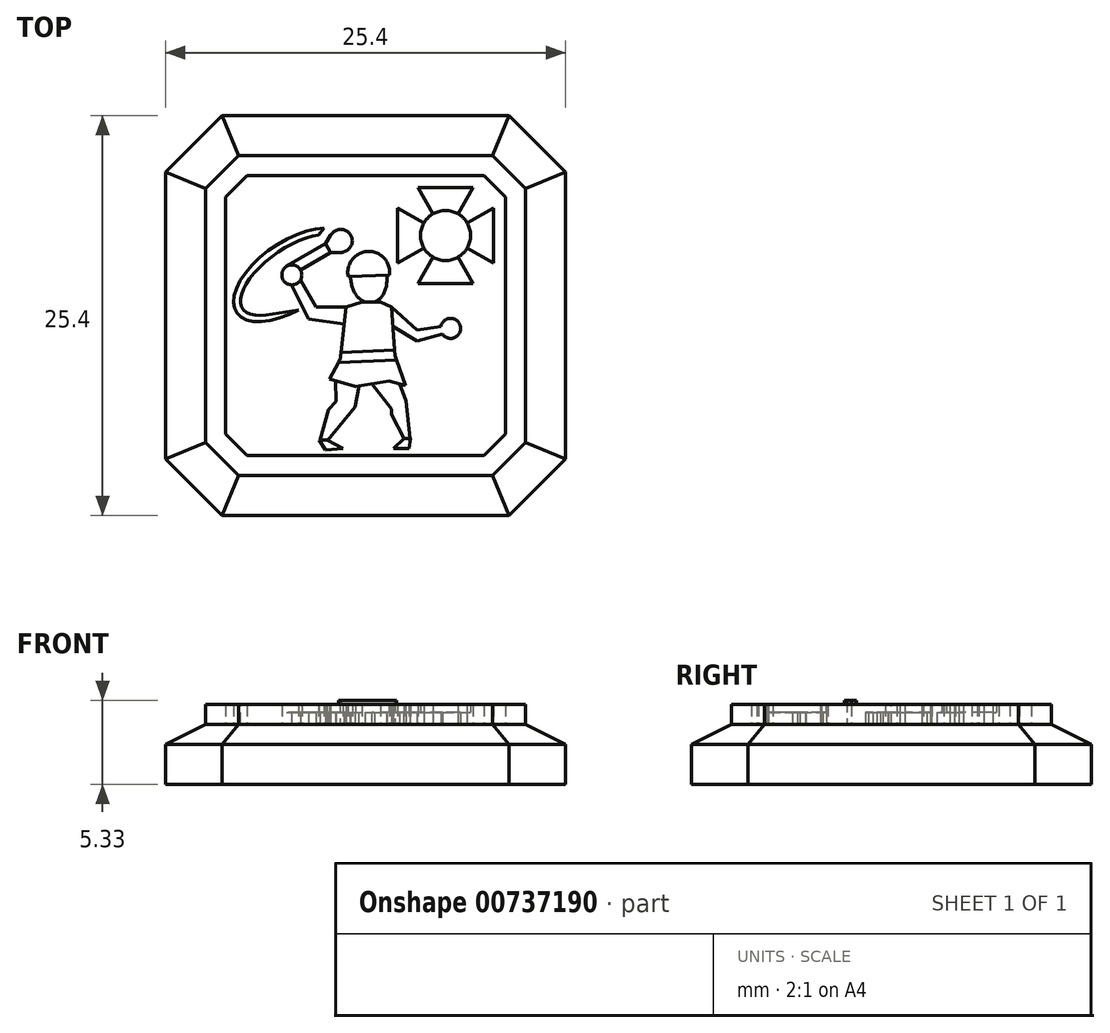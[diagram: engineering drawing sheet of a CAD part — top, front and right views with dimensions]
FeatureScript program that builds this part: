
annotation { "Feature Type Name" : "Feature", "Feature Type Description" : "" }
export const myFeature = defineFeature(function(context is Context, id is Id, definition is map)
    precondition{}
    {
        {
            var Q0;
            Q0=qCreatedBy(makeId("Top.planeOp"),FACE);
            var sketch = newSketch(context, id + "F0", { "sketchPlane" : qUnion([Q0])});
            skLineSegment(sketch, "E0", {"start": v(0, 34.78) * mm, "end": v(0, -32.67) * mm, "construction": true});
            skLineSegment(sketch, "E1", {"start": v(-47.17, 0) * mm, "end": v(41.3, 0) * mm});
            skLineSegment(sketch, "E2", {"start": v(0, 12.7) * mm, "end": v(-9.1, 12.7) * mm});
            skLineSegment(sketch, "E3", {"start": v(-9.1, 12.7) * mm, "end": v(-12.7, 9.1) * mm});
            skLineSegment(sketch, "E4", {"start": v(-12.7, 9.1) * mm, "end": v(-12.7, 0) * mm});
            skLineSegment(sketch, "E5.MirrorCS", {"start": v(0, 12.7) * mm, "end": v(9.1, 12.7) * mm});
            skLineSegment(sketch, "E6.MirrorCS", {"start": v(9.1, 12.7) * mm, "end": v(12.7, 9.1) * mm});
            skLineSegment(sketch, "E7.MirrorCS", {"start": v(12.7, 9.1) * mm, "end": v(12.7, 0) * mm});
            skLineSegment(sketch, "E8.MirrorCS", {"start": v(12.7, -9.1) * mm, "end": v(12.7, 0) * mm});
            skLineSegment(sketch, "E9.MirrorCS", {"start": v(9.1, -12.7) * mm, "end": v(12.7, -9.1) * mm});
            skLineSegment(sketch, "E10.MirrorCS", {"start": v(0, -12.7) * mm, "end": v(9.1, -12.7) * mm});
            skLineSegment(sketch, "E11.MirrorCS", {"start": v(0, -12.7) * mm, "end": v(-9.1, -12.7) * mm});
            skLineSegment(sketch, "E12.MirrorCS", {"start": v(-9.1, -12.7) * mm, "end": v(-12.7, -9.1) * mm});
            skLineSegment(sketch, "E13.MirrorCS", {"start": v(-12.7, -9.1) * mm, "end": v(-12.7, 0) * mm});
            skSolve(sketch);
        }
        {
            var Q0;
            Q0=makeQuery(id+"F0.imprint","IMPRINT",FACE,{"disambiguationData":[TD([[makeQuery(id+"F0.imprint","IMPRINT",EDGE,{"derivedFrom":sQuery(id+"F0.wireOp",EDGE,"E2")}),1.0]])]});
            var Q1;
            {var subQ0=sQuery(id+"F0.wireOp",EDGE,"E8.MirrorCS");Q1=makeQuery(id+"F0.imprint","IMPRINT",FACE,{"disambiguationData":[TD([[makeQuery(id+"F0.imprint","IMPRINT",EDGE,{"derivedFrom":subQ0}),1.0]])]});}
            extrude(context, id + "F1", {"entities" : qUnion([Q0, Q1]), "depth" : 3.8 * mm, "offsetDistance" : 25.4 * mm});
        }
        {
            var Q0;
            Q0=makeQuery(id+"F1.opExtrude","CAP_EDGE",EDGE,{"disambiguationData":[OSD([sQuery(id+"F0.wireOp",EDGE,"E10.MirrorCS"),sQuery(id+"F0.wireOp",EDGE,"E11.MirrorCS")])],"isStart":false});
            var Q1;
            Q1=makeQuery(id+"F1.opExtrude","CAP_EDGE",EDGE,{"disambiguationData":[OSD([sQuery(id+"F0.wireOp",EDGE,"E4"),sQuery(id+"F0.wireOp",EDGE,"E13.MirrorCS")])],"isStart":false});
            var Q2;
            Q2=makeQuery(id+"F1.opExtrude","CAP_EDGE",EDGE,{"disambiguationData":[OSD([sQuery(id+"F0.wireOp",EDGE,"E2"),sQuery(id+"F0.wireOp",EDGE,"E5.MirrorCS")])],"isStart":false});
            var Q3;
            Q3=makeQuery(id+"F1.opExtrude","CAP_EDGE",EDGE,{"disambiguationData":[OSD([sQuery(id+"F0.wireOp",EDGE,"E7.MirrorCS"),sQuery(id+"F0.wireOp",EDGE,"E8.MirrorCS")])],"isStart":false});
            var Q4;
            Q4=makeQuery(id+"F1.opExtrude","CAP_EDGE",EDGE,{"disambiguationData":[OSD([sQuery(id+"F0.wireOp",EDGE,"E6.MirrorCS")])],"isStart":false});
            var Q5;
            Q5=makeQuery(id+"F1.opExtrude","CAP_EDGE",EDGE,{"disambiguationData":[OSD([sQuery(id+"F0.wireOp",EDGE,"E3")])],"isStart":false});
            var Q6;
            Q6=makeQuery(id+"F1.opExtrude","CAP_EDGE",EDGE,{"disambiguationData":[OSD([sQuery(id+"F0.wireOp",EDGE,"E9.MirrorCS")])],"isStart":false});
            var Q7;
            Q7=makeQuery(id+"F1.opExtrude","CAP_EDGE",EDGE,{"disambiguationData":[OSD([sQuery(id+"F0.wireOp",EDGE,"E12.MirrorCS")])],"isStart":false});
            chamfer(context, id + "F2", {"entities" : qUnion([Q0, Q1, Q2, Q3, Q4, Q5, Q6, Q7]), "chamferType" : ChamferType.TWO_OFFSETS, "width1" : 1.27 * mm, "oppositeDirection" : false, "width2" : 2.54 * mm, "tangentPropagation" : true});
        }
        {
            var Q0;
            Q0=qCreatedBy(makeId("Top.planeOp"),FACE);
            var sketch = newSketch(context, id + "F3", { "sketchPlane" : qUnion([Q0])});
            skLineSegment(sketch, "E14", {"start": v(-10.16, 8.06) * mm, "end": v(-8.06, 10.16) * mm});
            skLineSegment(sketch, "E15", {"start": v(-8.06, 10.16) * mm, "end": v(0, 10.16) * mm});
            skLineSegment(sketch, "E16", {"start": v(-10.16, 8.06) * mm, "end": v(-10.16, 0) * mm});
            skLineSegment(sketch, "E17", {"start": v(-15.43, 0) * mm, "end": v(15.43, 0) * mm, "construction": true});
            skLineSegment(sketch, "E18", {"start": v(0, 15.6) * mm, "end": v(0, -14.81) * mm, "construction": true});
            skLineSegment(sketch, "E19.MirrorCS", {"start": v(8.06, 10.16) * mm, "end": v(0, 10.16) * mm});
            skLineSegment(sketch, "E20.MirrorCS", {"start": v(10.16, 8.06) * mm, "end": v(8.06, 10.16) * mm});
            skLineSegment(sketch, "E21.MirrorCS", {"start": v(10.16, 8.06) * mm, "end": v(10.16, 0) * mm});
            skLineSegment(sketch, "E22.MirrorCS", {"start": v(-10.16, -8.06) * mm, "end": v(-10.16, 0) * mm});
            skLineSegment(sketch, "E23.MirrorCS", {"start": v(-10.16, -8.06) * mm, "end": v(-8.06, -10.16) * mm});
            skLineSegment(sketch, "E24.MirrorCS", {"start": v(-8.06, -10.16) * mm, "end": v(0, -10.16) * mm});
            skLineSegment(sketch, "E25.MirrorCS", {"start": v(8.06, -10.16) * mm, "end": v(0, -10.16) * mm});
            skLineSegment(sketch, "E26.MirrorCS", {"start": v(10.16, -8.06) * mm, "end": v(8.06, -10.16) * mm});
            skLineSegment(sketch, "E27.MirrorCS", {"start": v(10.16, -8.06) * mm, "end": v(10.16, 0) * mm});
            skLineSegment(sketch, "E28", {"start": v(0, 8.9) * mm, "end": v(-7.53, 8.9) * mm});
            skLineSegment(sketch, "E29", {"start": v(-8.89, 7.53) * mm, "end": v(-8.89, 0) * mm});
            skLineSegment(sketch, "E30", {"start": v(-8.89, 7.53) * mm, "end": v(-7.53, 8.9) * mm});
            skLineSegment(sketch, "E31.MirrorCS", {"start": v(0, 8.9) * mm, "end": v(7.53, 8.9) * mm});
            skLineSegment(sketch, "E32.MirrorCS", {"start": v(8.89, 7.53) * mm, "end": v(7.53, 8.9) * mm});
            skLineSegment(sketch, "E33.MirrorCS", {"start": v(8.89, 7.53) * mm, "end": v(8.89, 0) * mm});
            skLineSegment(sketch, "E34.MirrorCS", {"start": v(-8.89, -7.53) * mm, "end": v(-8.89, 0) * mm});
            skLineSegment(sketch, "E35.MirrorCS", {"start": v(-8.89, -7.53) * mm, "end": v(-7.53, -8.9) * mm});
            skLineSegment(sketch, "E36.MirrorCS", {"start": v(0, -8.9) * mm, "end": v(-7.53, -8.9) * mm});
            skLineSegment(sketch, "E37.MirrorCS", {"start": v(0, -8.9) * mm, "end": v(7.53, -8.9) * mm});
            skLineSegment(sketch, "E38.MirrorCS", {"start": v(8.89, -7.53) * mm, "end": v(7.53, -8.9) * mm});
            skLineSegment(sketch, "E39.MirrorCS", {"start": v(8.89, -7.53) * mm, "end": v(8.89, 0) * mm});
            skSolve(sketch);
        }
        {
            var Q0;
            Q0=makeQuery(id+"F3.imprint","IMPRINT",FACE,{"disambiguationData":[TD([[makeQuery(id+"F3.imprint","IMPRINT",EDGE,{"derivedFrom":sQuery(id+"F3.wireOp",EDGE,"E14")}),-1.0]])]});
            extrude(context, id + "F4", {"entities" : qUnion([Q0]), "operationType" : NewBodyOperationType.ADD, "depth" : 5.08 * mm, "offsetDistance" : 25.4 * mm});
        }
        {
            var Q0;
            Q0=qCreatedBy(makeId("Top.planeOp"),FACE);
            var sketch = newSketch(context, id + "F5", { "sketchPlane" : qUnion([Q0])});
            skLineSegment(sketch, "E40", {"start": v(0, 7.92) * mm, "end": v(0, -7.63) * mm, "construction": true});
            skLineSegment(sketch, "E41", {"start": v(-5.02, 0) * mm, "end": v(8.7, 0) * mm, "construction": true});
            skLineSegment(sketch, "E42", {"start": v(-1.23, 0.54) * mm, "end": v(-3.14, 0.54) * mm});
            skLineSegment(sketch, "E43", {"start": v(-3.14, 0.54) * mm, "end": v(-4.13, 2.26) * mm});
            skLineSegment(sketch, "E44", {"start": v(-4.13, 2.9) * mm, "end": v(-2.2, 4) * mm});
            skLineSegment(sketch, "E45", {"start": v(-4.1, 3.28) * mm, "end": v(-0.46, 5.39) * mm, "construction": true});
            skLineSegment(sketch, "E46", {"start": v(-2.2, 4) * mm, "end": v(-1.57, 4) * mm});
            skArc(sketch, "E47", {"start": v(-1.57, 4) * mm, "mid": v(-0.94, 5.1) * mm, "end": v(-2.2, 5.1) * mm});
            skLineSegment(sketch, "E48.MirrorCS", {"start": v(-2.53, 4.56) * mm, "end": v(-2.2, 5.1) * mm});
            skLineSegment(sketch, "E49.MirrorCS", {"start": v(-4.73, 3.29) * mm, "end": v(-2.53, 4.56) * mm});
            skLineSegment(sketch, "E50", {"start": v(-4.73, 3.29) * mm, "end": v(-5, 3.13) * mm});
            skLineSegment(sketch, "E51", {"start": v(-4.68, 1.94) * mm, "end": v(-3.5, -0.1) * mm});
            skLineSegment(sketch, "E52", {"start": v(-3.5, -0.1) * mm, "end": v(-1.23, -0.1) * mm});
            skLineSegment(sketch, "E53", {"start": v(-5, 3.13) * mm, "end": v(-3.63, 0.75) * mm, "construction": true});
            skArc(sketch, "E54", {"start": v(-4.13, 2.26) * mm, "mid": v(-4.05, 2.58) * mm, "end": v(-4.13, 2.9) * mm});
            skPoint(sketch, "E55.orphan", {"position": v(-4.4, 2.74) * mm});
            skArc(sketch, "E56.trimOffspring", {"start": v(-5, 3.13) * mm, "mid": v(-5.3, 2.41) * mm, "end": v(-4.68, 1.94) * mm});
            skEllipticalArc(sketch, "E57", {});
            skLineSegment(sketch, "E58", {"start": v(-2.63, 5.55) * mm, "end": v(-2.98, 5.12) * mm});
            skLineSegment(sketch, "E59", {"start": v(-4.25, 0.36) * mm, "end": v(-6.33, 0.04) * mm});
            skEllipticalArc(sketch, "E60.trimOffspring", {});
            skPoint(sketch, "E61.orphan", {"position": v(-7.38, 0) * mm});
            skLineSegment(sketch, "E62", {"start": v(-1.23, 0.54) * mm, "end": v(-1.23, -0.1) * mm});
            skArc(sketch, "E63", {"start": v(-2.2, 5.1) * mm, "mid": v(-2.2, 4.37) * mm, "end": v(-1.57, 4) * mm});
            const initialGuessF5  = {"E57": [-0.0046837912392679445, 0.0025788224418153206, 0.8258157853669288, 0.5639399690027324, 0.004253587152070668, 0.0021255208665485244, 0.6540447710013154, 4.501058906339192], "E60.trimOffspring": [-0.0046837912392679445, 0.0025788224418153206, 0.8210613996496663, 0.5708398882395405, 0.0037873752104786293, 0.0016958796101459604, 0.7175157057819602, 3.8811688054549336]};
            skSetInitialGuess(sketch, initialGuessF5);
            skSolve(sketch);
        }
        {
            var Q0;
            Q0 = qSketchRegion(id + "F5", true);
            extrude(context, id + "F6", {"entities" : qUnion([Q0]), "operationType" : NewBodyOperationType.ADD, "depth" : 4.57 * mm, "offsetDistance" : 25.4 * mm});
        }
        {
            var Q0;
            Q0=qCreatedBy(makeId("Top.planeOp"),FACE);
            var sketch = newSketch(context, id + "F7", { "sketchPlane" : qUnion([Q0])});
            skLineSegment(sketch, "E64", {"start": v(-1.23, 0.54) * mm, "end": v(-1.23, -4.15) * mm, "construction": true});
            skLineSegment(sketch, "E65", {"start": v(-1.23, 0.54) * mm, "end": v(-1.61, -2.84) * mm});
            skLineSegment(sketch, "E66", {"start": v(-1.61, -2.84) * mm, "end": v(-2.28, -4.03) * mm});
            skLineSegment(sketch, "E67", {"start": v(-2.28, -4.03) * mm, "end": v(-0.63, -4.52) * mm});
            skLineSegment(sketch, "E68", {"start": v(-0.63, -4.52) * mm, "end": v(1.5, -4.16) * mm});
            skLineSegment(sketch, "E69", {"start": v(1.5, -4.16) * mm, "end": v(2.54, -4.44) * mm});
            skLineSegment(sketch, "E70", {"start": v(2.54, -4.44) * mm, "end": v(1.87, -2.55) * mm});
            skLineSegment(sketch, "E71", {"start": v(1.87, -2.55) * mm, "end": v(1.66, 0.54) * mm});
            skLineSegment(sketch, "E72", {"start": v(-1.23, 0.54) * mm, "end": v(-0.23, 0.85) * mm});
            skLineSegment(sketch, "E73", {"start": v(-0.23, 0.85) * mm, "end": v(0.96, 0.85) * mm});
            skLineSegment(sketch, "E74", {"start": v(0.96, 0.85) * mm, "end": v(1.66, 0.54) * mm});
            skSolve(sketch);
        }
        {
            var Q0;
            Q0 = qSketchRegion(id + "F7", true);
            extrude(context, id + "F8", {"entities" : qUnion([Q0]), "operationType" : NewBodyOperationType.ADD, "depth" : 5.08 * mm, "offsetDistance" : 25.4 * mm});
        }
        {
            var Q0;
            Q0=qCreatedBy(makeId("Top.planeOp"),FACE);
            var sketch = newSketch(context, id + "F9", { "sketchPlane" : qUnion([Q0])});
            skLineSegment(sketch, "E75", {"start": v(-1.91, -4.02) * mm, "end": v(-1.86, -5.47) * mm});
            skLineSegment(sketch, "E76", {"start": v(-2.9, -7.94) * mm, "end": v(-2.44, -7.94) * mm});
            skLineSegment(sketch, "E77", {"start": v(-2.44, -7.94) * mm, "end": v(-0.67, -5.82) * mm});
            skLineSegment(sketch, "E78", {"start": v(-0.67, -5.82) * mm, "end": v(-0.4, -4.37) * mm});
            skLineSegment(sketch, "E79", {"start": v(-0.4, -4.37) * mm, "end": v(-1.91, -4.02) * mm});
            skLineSegment(sketch, "E80", {"start": v(2.08, -4.15) * mm, "end": v(2.57, -5.42) * mm});
            skLineSegment(sketch, "E81", {"start": v(2.57, -5.42) * mm, "end": v(2.84, -7.86) * mm});
            skLineSegment(sketch, "E82", {"start": v(2.84, -7.86) * mm, "end": v(2.47, -7.86) * mm});
            skLineSegment(sketch, "E83", {"start": v(2.47, -7.86) * mm, "end": v(1.66, -6.28) * mm});
            skLineSegment(sketch, "E84", {"start": v(1.66, -6.28) * mm, "end": v(1.66, -5.95) * mm});
            skLineSegment(sketch, "E85", {"start": v(1.66, -5.95) * mm, "end": v(0.28, -4.16) * mm});
            skLineSegment(sketch, "E86", {"start": v(0.28, -4.16) * mm, "end": v(2.08, -4.15) * mm});
            skLineSegment(sketch, "E87", {"start": v(-1.86, -5.47) * mm, "end": v(-2.34, -5.97) * mm});
            skLineSegment(sketch, "E88", {"start": v(-2.34, -5.97) * mm, "end": v(-2.9, -7.94) * mm});
            skSolve(sketch);
        }
        {
            var Q0;
            Q0 = qSketchRegion(id + "F9", true);
            extrude(context, id + "F10", {"entities" : qUnion([Q0]), "operationType" : NewBodyOperationType.ADD, "depth" : 4.57 * mm, "offsetDistance" : 25.4 * mm});
        }
        {
            var Q0;
            Q0=qCreatedBy(makeId("Top.planeOp"),FACE);
            var sketch = newSketch(context, id + "F11", { "sketchPlane" : qUnion([Q0])});
            skCircle(sketch, "E89", {"center": v(5.08, 5.08) * mm, "radius": 1.59 * mm});
            skLineSegment(sketch, "E90", {"start": v(5.08, 8.81) * mm, "end": v(5.08, 1.61) * mm, "construction": true});
            skLineSegment(sketch, "E91", {"start": v(1.62, 5.08) * mm, "end": v(8.6, 5.08) * mm, "construction": true});
            skLineSegment(sketch, "E92", {"start": v(4.29, 6.45) * mm, "end": v(3.32, 8.13) * mm});
            skLineSegment(sketch, "E93", {"start": v(3.32, 8.13) * mm, "end": v(5.08, 8.13) * mm});
            skLineSegment(sketch, "E94", {"start": v(5.08, 5.08) * mm, "end": v(7.8, 2.36) * mm, "construction": true});
            skLineSegment(sketch, "E95.MirrorCS", {"start": v(6.84, 8.13) * mm, "end": v(5.08, 8.13) * mm});
            skLineSegment(sketch, "E96.MirrorCS", {"start": v(5.87, 6.45) * mm, "end": v(6.84, 8.13) * mm});
            skLineSegment(sketch, "E97.MirrorCS", {"start": v(5.87, 3.7) * mm, "end": v(6.84, 2.03) * mm});
            skLineSegment(sketch, "E98.MirrorCS", {"start": v(6.84, 2.03) * mm, "end": v(5.08, 2.03) * mm});
            skLineSegment(sketch, "E99.MirrorCS", {"start": v(3.32, 2.03) * mm, "end": v(5.08, 2.03) * mm});
            skLineSegment(sketch, "E100.MirrorCS", {"start": v(4.29, 3.7) * mm, "end": v(3.32, 2.03) * mm});
            skLineSegment(sketch, "E101.MirrorCS", {"start": v(6.45, 4.29) * mm, "end": v(8.13, 3.32) * mm});
            skLineSegment(sketch, "E102.MirrorCS", {"start": v(8.13, 3.32) * mm, "end": v(8.13, 5.08) * mm});
            skLineSegment(sketch, "E103.MirrorCS", {"start": v(8.13, 6.84) * mm, "end": v(8.13, 5.08) * mm});
            skLineSegment(sketch, "E104.MirrorCS", {"start": v(6.45, 5.87) * mm, "end": v(8.13, 6.84) * mm});
            skLineSegment(sketch, "E105.MirrorCS", {"start": v(3.7, 5.87) * mm, "end": v(2.03, 6.84) * mm});
            skLineSegment(sketch, "E106.MirrorCS", {"start": v(2.03, 6.84) * mm, "end": v(2.03, 5.08) * mm});
            skLineSegment(sketch, "E107.MirrorCS", {"start": v(2.03, 3.32) * mm, "end": v(2.03, 5.08) * mm});
            skLineSegment(sketch, "E108.MirrorCS", {"start": v(3.7, 4.29) * mm, "end": v(2.03, 3.32) * mm});
            skSolve(sketch);
        }
        {
            var Q0;
            {var subQ0=sQuery(id+"F11.wireOp",EDGE,"E89");var subQ4=makeQuery(id+"F11.imprint","INTERSECT",VERTEX,{"derivedFrom":[subQ0,sQuery(id+"F11.wireOp",EDGE,"E96.MirrorCS")]});Q0=makeQuery(id+"F11.imprint","IMPRINT",FACE,{"disambiguationData":[TD([[makeQuery(id+"F11.imprint","IMPRINT",EDGE,{"disambiguationData":[TD([[subQ4,1.0]])],"derivedFrom":subQ0}),1.0]])]});}
            extrude(context, id + "F12", {"entities" : qUnion([Q0]), "operationType" : NewBodyOperationType.ADD, "depth" : 4.57 * mm, "offsetDistance" : 25.4 * mm});
        }
        {
            var Q0;
            {var subQ0=sQuery(id+"F11.wireOp",EDGE,"E105.MirrorCS");Q0=makeQuery(id+"F11.imprint","IMPRINT",FACE,{"disambiguationData":[TD([[makeQuery(id+"F11.imprint","IMPRINT",EDGE,{"derivedFrom":subQ0}),1.0]])]});}
            var Q1;
            {var subQ0=sQuery(id+"F11.wireOp",EDGE,"E97.MirrorCS");Q1=makeQuery(id+"F11.imprint","IMPRINT",FACE,{"disambiguationData":[TD([[makeQuery(id+"F11.imprint","IMPRINT",EDGE,{"derivedFrom":subQ0}),-1.0]])]});}
            var Q2;
            {var subQ0=sQuery(id+"F11.wireOp",EDGE,"E92");Q2=makeQuery(id+"F11.imprint","IMPRINT",FACE,{"disambiguationData":[TD([[makeQuery(id+"F11.imprint","IMPRINT",EDGE,{"derivedFrom":subQ0}),-1.0]])]});}
            var Q3;
            {var subQ0=sQuery(id+"F11.wireOp",EDGE,"E101.MirrorCS");Q3=makeQuery(id+"F11.imprint","IMPRINT",FACE,{"disambiguationData":[TD([[makeQuery(id+"F11.imprint","IMPRINT",EDGE,{"derivedFrom":subQ0}),1.0]])]});}
            extrude(context, id + "F13", {"entities" : qUnion([Q0, Q1, Q2, Q3]), "operationType" : NewBodyOperationType.ADD, "depth" : 5.08 * mm, "offsetDistance" : 25.4 * mm});
        }
        {
            var Q0;
            Q0=qCreatedBy(makeId("Top.planeOp"),FACE);
            var sketch = newSketch(context, id + "F14", { "sketchPlane" : qUnion([Q0])});
            skLineSegment(sketch, "E109", {"start": v(1.66, 0.54) * mm, "end": v(3.27, -0.91) * mm});
            skLineSegment(sketch, "E110", {"start": v(3.27, -0.91) * mm, "end": v(4.78, -0.7) * mm});
            skLineSegment(sketch, "E111", {"start": v(4.88, -1.18) * mm, "end": v(3.26, -1.64) * mm});
            skLineSegment(sketch, "E112", {"start": v(3.26, -1.64) * mm, "end": v(1.74, -0.7) * mm});
            skArc(sketch, "E113", {"start": v(4.88, -1.18) * mm, "mid": v(6.02, -0.69) * mm, "end": v(4.78, -0.7) * mm});
            skPoint(sketch, "E114.orphan", {"position": v(5.46, -1.02) * mm});
            skPoint(sketch, "E115.start.orphan", {"position": v(5.35, -0.62) * mm});
            skLineSegment(sketch, "E116", {"start": v(1.66, 0.54) * mm, "end": v(1.74, -0.7) * mm});
            skSolve(sketch);
        }
        {
            var Q0;
            Q0 = qSketchRegion(id + "F14", true);
            extrude(context, id + "F15", {"entities" : qUnion([Q0]), "operationType" : NewBodyOperationType.ADD, "depth" : 4.57 * mm, "offsetDistance" : 25.4 * mm});
        }
        {
            var Q0;
            Q0=qCreatedBy(makeId("Top.planeOp"),FACE);
            var sketch = newSketch(context, id + "F16", { "sketchPlane" : qUnion([Q0])});
            skLineSegment(sketch, "E117", {"start": v(-1.35, -0.53) * mm, "end": v(-3.63, -0.21) * mm});
            skLineSegment(sketch, "E118", {"start": v(-3.63, -0.21) * mm, "end": v(-4.68, 1.94) * mm});
            skLineSegment(sketch, "E119", {"start": v(-4.68, 1.94) * mm, "end": v(-3.38, 0) * mm});
            skLineSegment(sketch, "E120", {"start": v(-3.38, 0) * mm, "end": v(-1.17, 0) * mm});
            skLineSegment(sketch, "E121", {"start": v(-1.17, 0) * mm, "end": v(-1.35, -0.53) * mm});
            skSolve(sketch);
        }
        {
            var Q0;
            Q0 = qSketchRegion(id + "F16", true);
            extrude(context, id + "F17", {"entities" : qUnion([Q0]), "operationType" : NewBodyOperationType.ADD, "depth" : 4.57 * mm, "offsetDistance" : 25.4 * mm});
        }
        {
            var Q0;
            Q0=qCreatedBy(makeId("Top.planeOp"),FACE);
            var sketch = newSketch(context, id + "F18", { "sketchPlane" : qUnion([Q0])});
            skLineSegment(sketch, "E122", {"start": v(2.45, -7.8) * mm, "end": v(1.76, -8.43) * mm});
            skLineSegment(sketch, "E123", {"start": v(1.76, -8.43) * mm, "end": v(2.75, -8.44) * mm});
            skLineSegment(sketch, "E124", {"start": v(2.75, -8.44) * mm, "end": v(2.87, -7.81) * mm});
            skLineSegment(sketch, "E125", {"start": v(2.87, -7.81) * mm, "end": v(2.87, -7.81) * mm});
            skLineSegment(sketch, "E126", {"start": v(2.87, -7.81) * mm, "end": v(2.45, -7.8) * mm});
            skLineSegment(sketch, "E127", {"start": v(-2.94, -7.91) * mm, "end": v(-2.54, -8.55) * mm});
            skLineSegment(sketch, "E128", {"start": v(-2.54, -8.55) * mm, "end": v(-1.43, -8.45) * mm});
            skLineSegment(sketch, "E129", {"start": v(-1.43, -8.45) * mm, "end": v(-2.44, -7.92) * mm});
            skLineSegment(sketch, "E130", {"start": v(-2.44, -7.92) * mm, "end": v(-2.94, -7.91) * mm});
            skSolve(sketch);
        }
        {
            var Q0;
            Q0 = qSketchRegion(id + "F18", true);
            extrude(context, id + "F19", {"entities" : qUnion([Q0]), "operationType" : NewBodyOperationType.ADD, "depth" : 5.08 * mm, "offsetDistance" : 25.4 * mm});
        }
        {
            var Q0;
            Q0=qCreatedBy(makeId("Top.planeOp"),FACE);
            var sketch = newSketch(context, id + "F20", { "sketchPlane" : qUnion([Q0])});
            skEllipse(sketch, "E131", {"center": v(0.2, 2.38) * mm, "majorRadius": 1.59 * mm, "minorRadius": 1.15 * mm, "majorAxis": v(0.1, -1)});
            skSolve(sketch);
        }
        {
            var Q0;
            Q0 = qSketchRegion(id + "F20", true);
            extrude(context, id + "F21", {"entities" : qUnion([Q0]), "operationType" : NewBodyOperationType.ADD, "depth" : 4.57 * mm, "offsetDistance" : 25.4 * mm});
        }
        {
            var Q0;
            Q0=qCreatedBy(makeId("Top.planeOp"),FACE);
            var sketch = newSketch(context, id + "F22", { "sketchPlane" : qUnion([Q0])});
            skArc(sketch, "E132", {"start": v(1.52, 2.56) * mm, "mid": v(0.17, 4.07) * mm, "end": v(-1.1, 2.49) * mm});
            skLineSegment(sketch, "E133", {"start": v(1.52, 2.56) * mm, "end": v(-1.1, 2.49) * mm});
            skSolve(sketch);
        }
        {
            var Q0;
            Q0 = qSketchRegion(id + "F22", true);
            extrude(context, id + "F23", {"entities" : qUnion([Q0]), "operationType" : NewBodyOperationType.ADD, "depth" : 5.08 * mm, "offsetDistance" : 25.4 * mm});
        }
        {
            var Q0;
            Q0=qCreatedBy(makeId("Top.planeOp"),FACE);
            var sketch = newSketch(context, id + "F24", { "sketchPlane" : qUnion([Q0])});
            skArc(sketch, "E134", {"start": v(-1.57, 4) * mm, "mid": v(-0.94, 5.1) * mm, "end": v(-2.2, 5.1) * mm});
            skLineSegment(sketch, "E135", {"start": v(-2.53, 4.56) * mm, "end": v(-2.2, 5.1) * mm});
            skLineSegment(sketch, "E136", {"start": v(-2.2, 4) * mm, "end": v(-1.57, 4) * mm});
            skLineSegment(sketch, "E137", {"start": v(-1.98, 4.13) * mm, "end": v(-1.98, 4.13) * mm});
            skLineSegment(sketch, "E138", {"start": v(-2.53, 4.56) * mm, "end": v(-2.2, 4) * mm});
            skSolve(sketch);
        }
        {
            var Q0;
            Q0 = qSketchRegion(id + "F24", true);
            extrude(context, id + "F25", {"entities" : qUnion([Q0]), "operationType" : NewBodyOperationType.ADD, "depth" : 5.08 * mm, "offsetDistance" : 25.4 * mm});
        }
        {
            var Q0;
            Q0=makeQuery(id+"F6.opExtrude","CAP_FACE",FACE,{"disambiguationData":[OSD([sQuery(id+"F5.wireOp",EDGE,"E57"),sQuery(id+"F5.wireOp",EDGE,"E58"),sQuery(id+"F5.wireOp",EDGE,"E59"),sQuery(id+"F5.wireOp",EDGE,"E60.trimOffspring")])],"isStart":false});
            extrude(context, id + "F26", {"entities" : qUnion([Q0]), "operationType" : NewBodyOperationType.ADD, "depth" : 0.5 * mm, "offsetDistance" : 25.4 * mm});
        }
        {
            var Q0;
            Q0=makeQuery(id+"F17.boolean.opBoolean","MERGE",FACE,{"derivedFrom":[makeQuery(id+"F6.opExtrude","CAP_FACE",FACE,{"disambiguationData":[OSD([sQuery(id+"F5.wireOp",EDGE,"E42"),sQuery(id+"F5.wireOp",EDGE,"E43"),sQuery(id+"F5.wireOp",EDGE,"E44"),sQuery(id+"F5.wireOp",EDGE,"E46"),sQuery(id+"F5.wireOp",EDGE,"E47"),sQuery(id+"F5.wireOp",EDGE,"E48.MirrorCS"),sQuery(id+"F5.wireOp",EDGE,"E49.MirrorCS"),sQuery(id+"F5.wireOp",EDGE,"E50"),sQuery(id+"F5.wireOp",EDGE,"E51"),sQuery(id+"F5.wireOp",EDGE,"E52"),sQuery(id+"F5.wireOp",EDGE,"E54"),sQuery(id+"F5.wireOp",EDGE,"E56.trimOffspring"),sQuery(id+"F5.wireOp",EDGE,"E62")])],"isStart":false}),makeQuery(id+"F17.opExtrude","CAP_FACE",FACE,{"disambiguationData":[OSD([sQuery(id+"F16.wireOp",EDGE,"E117"),sQuery(id+"F16.wireOp",EDGE,"E118"),sQuery(id+"F16.wireOp",EDGE,"E119"),sQuery(id+"F16.wireOp",EDGE,"E120"),sQuery(id+"F16.wireOp",EDGE,"E121")])],"isStart":false})]});
            var sketch = newSketch(context, id + "F27", { "sketchPlane" : qUnion([Q0])});
            skCircle(sketch, "E139", {"center": v(-4.68, 2.58) * mm, "radius": 0.64 * mm});
            skSolve(sketch);
        }
        {
            var Q0;
            Q0 = qSketchRegion(id + "F27", true);
            extrude(context, id + "F28", {"entities" : qUnion([Q0]), "operationType" : NewBodyOperationType.ADD, "depth" : 0.5 * mm, "offsetDistance" : 25.4 * mm});
        }
        {
            var Q0;
            Q0=makeQuery(id+"F8.opExtrude","CAP_FACE",FACE,{"disambiguationData":[OSD([sQuery(id+"F7.wireOp",EDGE,"E65"),sQuery(id+"F7.wireOp",EDGE,"E66"),sQuery(id+"F7.wireOp",EDGE,"E67"),sQuery(id+"F7.wireOp",EDGE,"E68"),sQuery(id+"F7.wireOp",EDGE,"E69"),sQuery(id+"F7.wireOp",EDGE,"E70"),sQuery(id+"F7.wireOp",EDGE,"E71"),sQuery(id+"F7.wireOp",EDGE,"E72"),sQuery(id+"F7.wireOp",EDGE,"E73"),sQuery(id+"F7.wireOp",EDGE,"E74")])],"isStart":false});
            var sketch = newSketch(context, id + "F29", { "sketchPlane" : qUnion([Q0])});
            skLineSegment(sketch, "E140", {"start": v(-1.7, -3) * mm, "end": v(1.97, -2.84) * mm});
            skLineSegment(sketch, "E141", {"start": v(1.97, -2.84) * mm, "end": v(1.87, -2.55) * mm});
            skLineSegment(sketch, "E142", {"start": v(1.87, -2.55) * mm, "end": v(1.85, -2.2) * mm});
            skLineSegment(sketch, "E143", {"start": v(1.85, -2.2) * mm, "end": v(-1.56, -2.36) * mm});
            skLineSegment(sketch, "E144", {"start": v(-1.56, -2.36) * mm, "end": v(-1.61, -2.84) * mm});
            skLineSegment(sketch, "E145", {"start": v(-1.61, -2.84) * mm, "end": v(-1.7, -3) * mm});
            skPoint(sketch, "E146.startSnap0", {"position": v(0.44, -4.34) * mm});
            skSolve(sketch);
        }
        {
            var Q0;
            {var subQ1=sQuery(id+"F29.wireOp",EDGE,"E144");Q0=makeQuery(id+"F29.imprint","IMPRINT",FACE,{"disambiguationData":[TD([[makeQuery(id+"F29.imprint","IMPRINT",EDGE,{"derivedFrom":subQ1}),1.0]])]});}
            var Q1;
            {var subQ3=sQuery(id+"F29.wireOp",EDGE,"E141");Q1=makeQuery(id+"F29.imprint","IMPRINT",FACE,{"disambiguationData":[TD([[makeQuery(id+"F29.imprint","IMPRINT",EDGE,{"derivedFrom":subQ3}),1.0]])]});}
            extrude(context, id + "F30", {"entities" : qUnion([Q0, Q1]), "operationType" : NewBodyOperationType.ADD, "depth" : 0.25 * mm, "offsetDistance" : 25.4 * mm});
        }
    });
